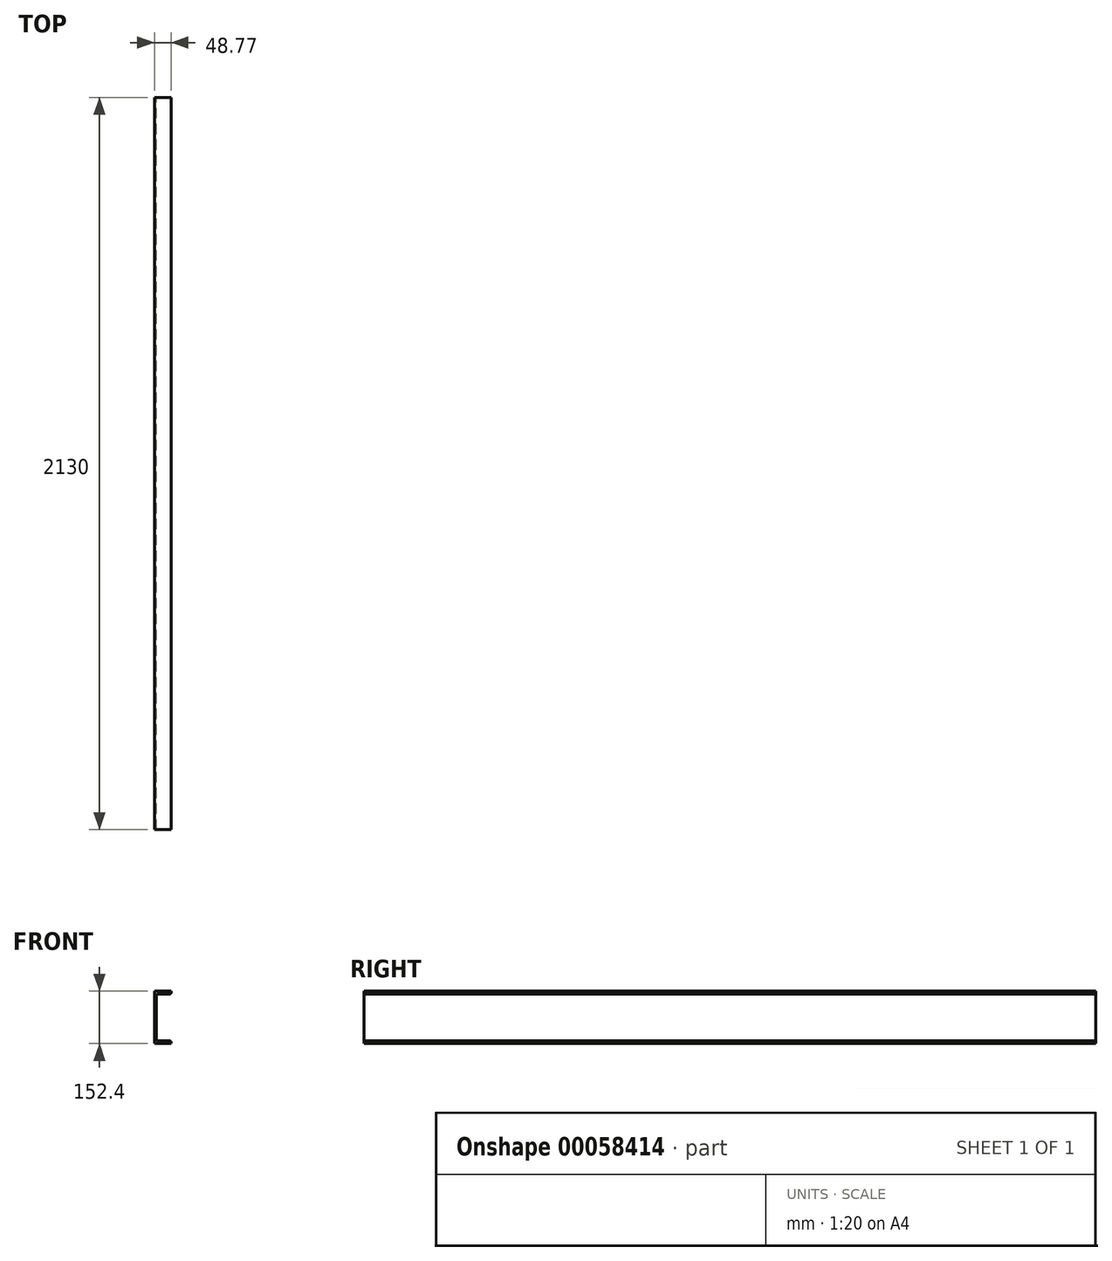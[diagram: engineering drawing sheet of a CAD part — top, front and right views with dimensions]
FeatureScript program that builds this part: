
annotation { "Feature Type Name" : "Feature", "Feature Type Description" : "" }
export const myFeature = defineFeature(function(context is Context, id is Id, definition is map)
    precondition{}
    {
        {
            var Q0;
            Q0=qCreatedBy(makeId("Front.planeOp"),FACE);
            var sketch = newSketch(context, id + "F0", { "sketchPlane" : qUnion([Q0])});
            skLineSegment(sketch, "E0", {"start": v(0, 76.2) * mm, "end": v(48.77, 76.2) * mm});
            skLineSegment(sketch, "E1", {"start": v(48.77, 76.2) * mm, "end": v(48.77, 67.49) * mm});
            skLineSegment(sketch, "E2", {"start": v(48.77, 67.49) * mm, "end": v(5.08, 67.49) * mm});
            skLineSegment(sketch, "E3", {"start": v(5.08, 67.49) * mm, "end": v(5.08, 0) * mm});
            skLineSegment(sketch, "E4", {"start": v(5.08, 0) * mm, "end": v(0, 0) * mm});
            skLineSegment(sketch, "E5", {"start": v(0, 0) * mm, "end": v(0, 76.2) * mm});
            skLineSegment(sketch, "E6.MirrorCS", {"start": v(5.08, -67.49) * mm, "end": v(5.08, 0) * mm});
            skLineSegment(sketch, "E7.MirrorCS", {"start": v(48.77, -67.49) * mm, "end": v(5.08, -67.49) * mm});
            skLineSegment(sketch, "E8.MirrorCS", {"start": v(48.77, -76.2) * mm, "end": v(48.77, -67.49) * mm});
            skLineSegment(sketch, "E9.MirrorCS", {"start": v(0, -76.2) * mm, "end": v(48.77, -76.2) * mm});
            skLineSegment(sketch, "E10.MirrorCS", {"start": v(0, 0) * mm, "end": v(0, -76.2) * mm});
            skSolve(sketch);
        }
        {
            var Q0;
            Q0=makeQuery(id+"F0.imprint","IMPRINT",FACE,{"disambiguationData":[TD([[makeQuery(id+"F0.imprint","IMPRINT",EDGE,{"derivedFrom":sQuery(id+"F0.wireOp",EDGE,"E0")}),-1.0]])]});
            var Q1;
            Q1=makeQuery(id+"F0.imprint","IMPRINT",FACE,{"disambiguationData":[TD([[makeQuery(id+"F0.imprint","IMPRINT",EDGE,{"derivedFrom":sQuery(id+"F0.wireOp",EDGE,"E4")}),1.0]])]});
            extrude(context, id + "F1", {"entities" : qUnion([Q0, Q1]), "depth" : 2130 * mm});
        }
        {
            var Q0;
            Q0=makeQuery(id+"F1.opExtrude","SWEPT_EDGE",EDGE,{"disambiguationData":[OSD([sQuery(id+"F0.wireOp",EDGE,"E6.MirrorCS"),sQuery(id+"F0.wireOp",EDGE,"E7.MirrorCS")])]});
            var Q1;
            Q1=makeQuery(id+"F1.opExtrude","SWEPT_EDGE",EDGE,{"disambiguationData":[OSD([sQuery(id+"F0.wireOp",EDGE,"E2"),sQuery(id+"F0.wireOp",EDGE,"E3")])]});
            fillet(context, id + "F2", {"entities" : qUnion([Q0, Q1]), "radius" : 5.08 * mm, "tangentPropagation" : true, "allowEdgeOverflow" : false});
        }
        {
            var Q0;
            Q0=makeQuery(id+"F1.opExtrude","SWEPT_EDGE",EDGE,{"disambiguationData":[OSD([sQuery(id+"F0.wireOp",EDGE,"E1"),sQuery(id+"F0.wireOp",EDGE,"E2")])]});
            var Q1;
            Q1=makeQuery(id+"F1.opExtrude","SWEPT_EDGE",EDGE,{"disambiguationData":[OSD([sQuery(id+"F0.wireOp",EDGE,"E7.MirrorCS"),sQuery(id+"F0.wireOp",EDGE,"E8.MirrorCS")])]});
            fillet(context, id + "F3", {"entities" : qUnion([Q0, Q1]), "radius" : 5.08 * mm, "tangentPropagation" : true, "allowEdgeOverflow" : false});
        }
    });
